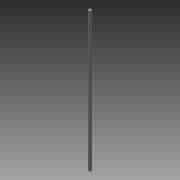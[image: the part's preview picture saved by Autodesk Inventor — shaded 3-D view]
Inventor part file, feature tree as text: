
AUTODESK INVENTOR PART (.ipt)
format: ipt  version: 2013 SP2 (Build 170200200, 200)  size: 60,928 bytes
history: native  units: mm
features: extrude x1, sketch x1
ambient origin geometry x8: Origin, YZ Plane, XZ Plane, XY Plane, X Axis, Y Axis, Z Axis, Center Point
bodies: Solid1 (feature_tree)
feature tree (2):
  extrude  "Extrusion1"  Depth=380.0mm TaperAngle=0.0deg
  sketch  "Sketch1"  dims[d0=8.0mm d1=380.0mm d2=0.0mm]
